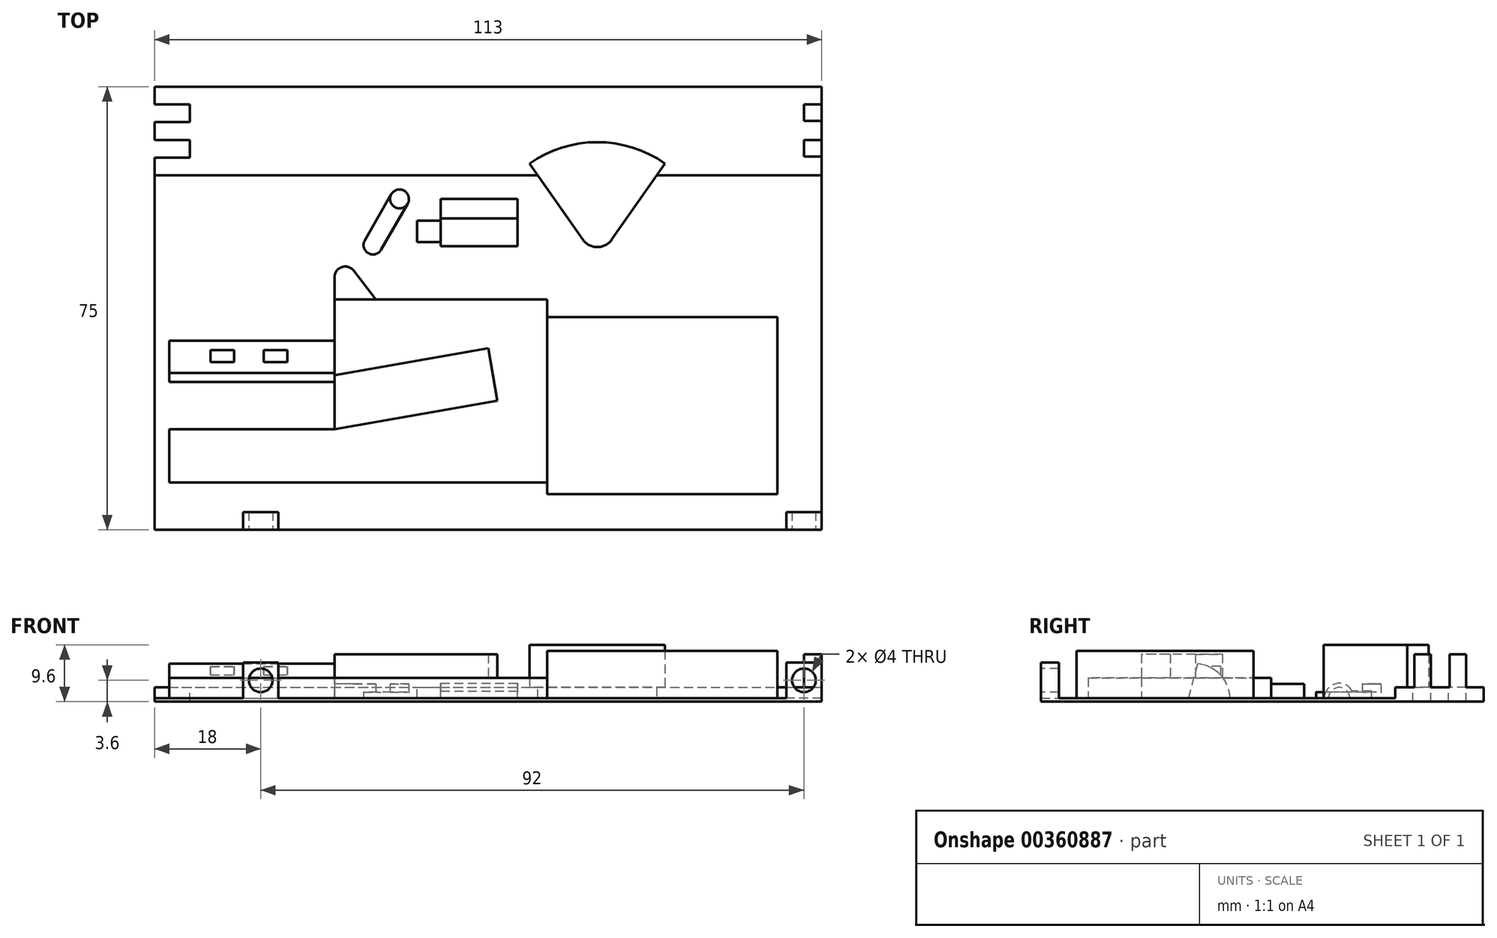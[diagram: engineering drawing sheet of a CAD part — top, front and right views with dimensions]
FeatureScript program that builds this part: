
annotation { "Feature Type Name" : "Feature", "Feature Type Description" : "" }
export const myFeature = defineFeature(function(context is Context, id is Id, definition is map)
    precondition{}
    {
        {
            var Q0;
            Q0=qCreatedBy(makeId("Top.planeOp"),FACE);
            var sketch = newSketch(context, id + "F0", { "sketchPlane" : qUnion([Q0])});
            skLineSegment(sketch, "E0.bottom", {"start": v(-56.5, 75) * mm, "end": v(56.5, 75) * mm});
            skLineSegment(sketch, "E0.top", {"start": v(-56.5, 0) * mm, "end": v(56.5, 0) * mm});
            skLineSegment(sketch, "E0.left", {"start": v(-56.5, 75) * mm, "end": v(-56.5, 0) * mm});
            skLineSegment(sketch, "E0.right", {"start": v(56.5, 75) * mm, "end": v(56.5, 0) * mm});
            skPoint(sketch, "E1", {"position": v(0, 0) * mm});
            skSolve(sketch);
        }
        {
            var Q0;
            Q0 = qSketchRegion(id + "F0", true);
            extrude(context, id + "F1", {"entities" : qUnion([Q0]), "depth" : 0.6 * mm});
        }
        {
            var Q0;
            Q0=makeQuery(id+"F1.opExtrude","CAP_FACE",FACE,{"disambiguationData":[OSD([sQuery(id+"F0.wireOp",EDGE,"E0.bottom"),sQuery(id+"F0.wireOp",EDGE,"E0.top"),sQuery(id+"F0.wireOp",EDGE,"E0.left"),sQuery(id+"F0.wireOp",EDGE,"E0.right")])],"isStart":false});
            var sketch = newSketch(context, id + "F2", { "sketchPlane" : qUnion([Q0])});
            skLineSegment(sketch, "E2.bottom", {"start": v(-56.5, 75) * mm, "end": v(56.5, 75) * mm});
            skLineSegment(sketch, "E2.top", {"start": v(-56.5, 60) * mm, "end": v(56.5, 60) * mm});
            skLineSegment(sketch, "E2.left", {"start": v(-56.5, 75) * mm, "end": v(-56.5, 60) * mm});
            skLineSegment(sketch, "E2.right", {"start": v(56.5, 75) * mm, "end": v(56.5, 60) * mm});
            skSolve(sketch);
        }
        {
            var Q0;
            Q0 = qSketchRegion(id + "F2", true);
            extrude(context, id + "F3", {"entities" : qUnion([Q0]), "operationType" : NewBodyOperationType.ADD, "depth" : 1.8 * mm});
        }
        {
            var Q0;
            Q0=qCreatedBy(makeId("Right.planeOp"),FACE);
            cPlane(context, id + "F4", {"entities" : qUnion([Q0]), "cplaneType" : CPlaneType.OFFSET, "offset" : 10 * mm, "width" : 150 * mm, "height" : 150 * mm});
        }
        {
            var Q0;
            Q0=qCreatedBy(id+"F4.planeOp",FACE);
            var sketch = newSketch(context, id + "F5", { "sketchPlane" : qUnion([Q0])});
            skLineSegment(sketch, "E3", {"start": v(6, 0.6) * mm, "end": v(36, 0.6) * mm});
            skLineSegment(sketch, "E4", {"start": v(36, 0.6) * mm, "end": v(36, 8.6) * mm});
            skLineSegment(sketch, "E5", {"start": v(6, 8.6) * mm, "end": v(6, 0.6) * mm});
            skLineSegment(sketch, "E6", {"start": v(36, 8.6) * mm, "end": v(6, 8.6) * mm});
            skSolve(sketch);
        }
        {
            var Q0;
            Q0 = qSketchRegion(id + "F5", true);
            extrude(context, id + "F6", {"entities" : qUnion([Q0]), "operationType" : NewBodyOperationType.ADD, "depth" : 39 * mm});
        }
        {
            var Q0;
            Q0=makeQuery(id+"F1.opExtrude","CAP_FACE",FACE,{"disambiguationData":[OSD([sQuery(id+"F0.wireOp",EDGE,"E0.bottom"),sQuery(id+"F0.wireOp",EDGE,"E0.top"),sQuery(id+"F0.wireOp",EDGE,"E0.left"),sQuery(id+"F0.wireOp",EDGE,"E0.right")])],"isStart":false});
            var sketch = newSketch(context, id + "F7", { "sketchPlane" : qUnion([Q0])});
            skLineSegment(sketch, "E7", {"start": v(-54, 17) * mm, "end": v(-54, 8) * mm});
            skLineSegment(sketch, "E8", {"start": v(-54, 8) * mm, "end": v(10, 8) * mm});
            skLineSegment(sketch, "E9", {"start": v(10, 8) * mm, "end": v(10, 39) * mm});
            skLineSegment(sketch, "E10", {"start": v(10, 39) * mm, "end": v(-26, 39) * mm});
            skLineSegment(sketch, "E11", {"start": v(-26, 39) * mm, "end": v(-26, 17) * mm});
            skLineSegment(sketch, "E12", {"start": v(-26, 17) * mm, "end": v(-54, 17) * mm});
            skSolve(sketch);
        }
        {
            var Q0;
            Q0 = qSketchRegion(id + "F7", true);
            extrude(context, id + "F8", {"entities" : qUnion([Q0]), "operationType" : NewBodyOperationType.ADD, "depth" : 3.4 * mm});
        }
        {
            var Q0;
            Q0=makeQuery(id+"F8.opExtrude","CAP_FACE",FACE,{"disambiguationData":[OSD([sQuery(id+"F7.wireOp",EDGE,"E7"),sQuery(id+"F7.wireOp",EDGE,"E8"),sQuery(id+"F7.wireOp",EDGE,"E9"),sQuery(id+"F7.wireOp",EDGE,"uyQ6YQ2C-q6pP-OxL6-5fo1-xEx53bqn0l92"),sQuery(id+"F7.wireOp",EDGE,"j48iJAs0-QAIT-l2oA-MukY-UUH54dbWInNL"),sQuery(id+"F7.wireOp",EDGE,"E10"),sQuery(id+"F7.wireOp",EDGE,"E11"),sQuery(id+"F7.wireOp",EDGE,"E12")])],"isStart":false});
            var sketch = newSketch(context, id + "F9", { "sketchPlane" : qUnion([Q0])});
            skLineSegment(sketch, "E13", {"start": v(-26, 17) * mm, "end": v(-26, 26.14) * mm});
            skLineSegment(sketch, "E14", {"start": v(-26, 26.14) * mm, "end": v(0.01, 30.73) * mm});
            skLineSegment(sketch, "E15", {"start": v(0.01, 30.73) * mm, "end": v(1.57, 21.86) * mm});
            skLineSegment(sketch, "E16", {"start": v(1.57, 21.86) * mm, "end": v(-26, 17) * mm});
            skSolve(sketch);
        }
        {
            var Q0;
            Q0 = qSketchRegion(id + "F9", true);
            extrude(context, id + "F10", {"entities" : qUnion([Q0]), "operationType" : NewBodyOperationType.ADD, "depth" : 4 * mm});
        }
        {
            var Q0;
            Q0=makeQuery(id+"F1.opExtrude","CAP_FACE",FACE,{"disambiguationData":[OSD([sQuery(id+"F0.wireOp",EDGE,"E0.bottom"),sQuery(id+"F0.wireOp",EDGE,"E0.top"),sQuery(id+"F0.wireOp",EDGE,"E0.left"),sQuery(id+"F0.wireOp",EDGE,"E0.right")])],"isStart":false});
            var sketch = newSketch(context, id + "F11", { "sketchPlane" : qUnion([Q0])});
            skLineSegment(sketch, "E17", {"start": v(-19, 39) * mm, "end": v(-26, 39) * mm});
            skLineSegment(sketch, "E18", {"start": v(-26, 39) * mm, "end": v(-26, 42.75) * mm});
            skLineSegment(sketch, "E19", {"start": v(-22.78, 43.86) * mm, "end": v(-19, 39) * mm});
            skPoint(sketch, "E20.visualSharp", {"position": v(-26, 48) * mm});
            skArc(sketch, "E20.filletArc", {"start": v(-22.78, 43.86) * mm, "mid": v(-24.78, 44.46) * mm, "end": v(-26, 42.75) * mm});
            skSolve(sketch);
        }
        {
            var Q0;
            Q0 = qSketchRegion(id + "F11", true);
            extrude(context, id + "F12", {"entities" : qUnion([Q0]), "operationType" : NewBodyOperationType.ADD, "depth" : 2.4 * mm});
        }
        {
            var Q0;
            Q0=makeQuery(id+"F12.boolean.opBoolean","MERGE",FACE,{"derivedFrom":[makeQuery(id+"F10.boolean.opBoolean","MERGE",FACE,{"derivedFrom":[makeQuery(id+"F8.opExtrude","SWEPT_FACE",FACE,{"disambiguationData":[OSD([sQuery(id+"F7.wireOp",EDGE,"E11")])]}),makeQuery(id+"F10.opExtrude","SWEPT_FACE",FACE,{"disambiguationData":[OSD([sQuery(id+"F9.wireOp",EDGE,"E13")])]})]}),makeQuery(id+"F12.opExtrude","SWEPT_FACE",FACE,{"disambiguationData":[OSD([sQuery(id+"F11.wireOp",EDGE,"E18")])]})]});
            var sketch = newSketch(context, id + "F13", { "sketchPlane" : qUnion([Q0])});
            skLineSegment(sketch, "E21", {"start": v(-32, 0.6) * mm, "end": v(-25, 0.6) * mm});
            skLineSegment(sketch, "E22", {"start": v(-25, 0.6) * mm, "end": v(-26.55, 6.4) * mm});
            skArc(sketch, "E23", {"start": v(-26.55, 6.4) * mm, "mid": v(-30.37, 4.53) * mm, "end": v(-32, 0.6) * mm});
            skSolve(sketch);
        }
        {
            var Q0;
            Q0 = qSketchRegion(id + "F13", true);
            extrude(context, id + "F14", {"entities" : qUnion([Q0]), "operationType" : NewBodyOperationType.ADD, "depth" : 28 * mm});
        }
        {
            var Q0;
            Q0=makeQuery(id+"F1.opExtrude","CAP_FACE",FACE,{"disambiguationData":[OSD([sQuery(id+"F0.wireOp",EDGE,"E0.bottom"),sQuery(id+"F0.wireOp",EDGE,"E0.top"),sQuery(id+"F0.wireOp",EDGE,"E0.left"),sQuery(id+"F0.wireOp",EDGE,"E0.right")])],"isStart":false});
            var sketch = newSketch(context, id + "F15", { "sketchPlane" : qUnion([Q0])});
            skLineSegment(sketch, "E24.bottom", {"start": v(-47, 30.4) * mm, "end": v(-43, 30.4) * mm});
            skLineSegment(sketch, "E24.top", {"start": v(-47, 28.4) * mm, "end": v(-43, 28.4) * mm});
            skLineSegment(sketch, "E24.left", {"start": v(-47, 30.4) * mm, "end": v(-47, 28.4) * mm});
            skLineSegment(sketch, "E24.right", {"start": v(-43, 30.4) * mm, "end": v(-43, 28.4) * mm});
            skLineSegment(sketch, "E25.bottom", {"start": v(-38, 30.4) * mm, "end": v(-34, 30.4) * mm});
            skLineSegment(sketch, "E25.top", {"start": v(-38, 28.4) * mm, "end": v(-34, 28.4) * mm});
            skLineSegment(sketch, "E25.left", {"start": v(-38, 30.4) * mm, "end": v(-38, 28.4) * mm});
            skLineSegment(sketch, "E25.right", {"start": v(-34, 30.4) * mm, "end": v(-34, 28.4) * mm});
            skSolve(sketch);
        }
        {
            var Q0;
            Q0 = qSketchRegion(id + "F15", true);
            extrude(context, id + "F16", {"entities" : qUnion([Q0]), "operationType" : NewBodyOperationType.ADD, "depth" : 5.4 * mm});
        }
        {
            var Q0;
            Q0=makeQuery(id+"F1.opExtrude","CAP_FACE",FACE,{"disambiguationData":[OSD([sQuery(id+"F0.wireOp",EDGE,"E0.bottom"),sQuery(id+"F0.wireOp",EDGE,"E0.top"),sQuery(id+"F0.wireOp",EDGE,"E0.left"),sQuery(id+"F0.wireOp",EDGE,"E0.right")])],"isStart":false});
            var sketch = newSketch(context, id + "F17", { "sketchPlane" : qUnion([Q0])});
            skLineSegment(sketch, "E26", {"start": v(29.97, 62) * mm, "end": v(18.5, 45.62) * mm});
            skLineSegment(sketch, "E27", {"start": v(18.5, 45.62) * mm, "end": v(7.03, 62) * mm});
            skArc(sketch, "E28", {"start": v(29.97, 62) * mm, "mid": v(18.5, 65.62) * mm, "end": v(7.03, 62) * mm});
            skSolve(sketch);
        }
        {
            var Q0;
            Q0 = qSketchRegion(id + "F17", true);
            extrude(context, id + "F18", {"entities" : qUnion([Q0]), "operationType" : NewBodyOperationType.ADD, "depth" : 9 * mm});
        }
        {
            var Q0;
            Q0=makeQuery(id+"F18.opExtrude","SWEPT_EDGE",EDGE,{"disambiguationData":[OSD([sQuery(id+"F17.wireOp",EDGE,"E26"),sQuery(id+"F17.wireOp",EDGE,"E27")])]});
            fillet(context, id + "F19", {"entities" : qUnion([Q0]), "radius" : 3 * mm, "tangentPropagation" : true, "allowEdgeOverflow" : false});
        }
        {
            var Q0;
            Q0=qCreatedBy(makeId("Right.planeOp"),FACE);
            cPlane(context, id + "F20", {"entities" : qUnion([Q0]), "cplaneType" : CPlaneType.OFFSET, "offset" : 5 * mm, "width" : 150 * mm, "height" : 150 * mm});
        }
        {
            var Q0;
            Q0=qCreatedBy(id+"F20.planeOp",FACE);
            var sketch = newSketch(context, id + "F21", { "sketchPlane" : qUnion([Q0])});
            skArc(sketch, "E29", {"start": v(52.93, 0) * mm, "mid": v(50.5, 3.1) * mm, "end": v(48.07, 0) * mm});
            skLineSegment(sketch, "E30", {"start": v(53, 0.6) * mm, "end": v(56, 0.6) * mm});
            skLineSegment(sketch, "E31", {"start": v(56, 0.6) * mm, "end": v(56, 1.8) * mm});
            skLineSegment(sketch, "E32", {"start": v(56, 1.8) * mm, "end": v(52.7, 1.8) * mm});
            skLineSegment(sketch, "E33", {"start": v(48.07, 0) * mm, "end": v(52.93, 0) * mm});
            skSolve(sketch);
        }
        {
            var Q0;
            Q0 = qSketchRegion(id + "F21", true);
            extrude(context, id + "F22", {"entities" : qUnion([Q0]), "operationType" : NewBodyOperationType.ADD, "oppositeDirection" : true, "depth" : 13 * mm});
        }
        {
            var Q0;
            Q0=makeQuery(id+"F22.opExtrude","CAP_FACE",FACE,{"disambiguationData":[OSD([sQuery(id+"F21.wireOp",EDGE,"E29"),sQuery(id+"F21.wireOp",EDGE,"E30"),sQuery(id+"F21.wireOp",EDGE,"E31"),sQuery(id+"F21.wireOp",EDGE,"E32")])],"isStart":false});
            var sketch = newSketch(context, id + "F23", { "sketchPlane" : qUnion([Q0])});
            skArc(sketch, "E34", {"start": v(-48.8, 0) * mm, "mid": v(-50.5, 2.4) * mm, "end": v(-52.2, 0) * mm});
            skLineSegment(sketch, "E35", {"start": v(-48.8, 0) * mm, "end": v(-52.2, 0) * mm});
            skSolve(sketch);
        }
        {
            var Q0;
            Q0 = qSketchRegion(id + "F23", true);
            extrude(context, id + "F24", {"entities" : qUnion([Q0]), "operationType" : NewBodyOperationType.ADD, "depth" : 4 * mm});
        }
        {
            var Q0;
            Q0=makeQuery(id+"F1.opExtrude","CAP_FACE",FACE,{"disambiguationData":[OSD([sQuery(id+"F0.wireOp",EDGE,"E0.bottom"),sQuery(id+"F0.wireOp",EDGE,"E0.top"),sQuery(id+"F0.wireOp",EDGE,"E0.left"),sQuery(id+"F0.wireOp",EDGE,"E0.right")])],"isStart":false});
            var sketch = newSketch(context, id + "F25", { "sketchPlane" : qUnion([Q0])});
            skCircle(sketch, "E36", {"center": v(-15, 56) * mm, "radius": 1.6 * mm});
            skSolve(sketch);
        }
        {
            var Q0;
            Q0 = qSketchRegion(id + "F25", true);
            extrude(context, id + "F26", {"entities" : qUnion([Q0]), "operationType" : NewBodyOperationType.ADD, "depth" : 2.4 * mm});
        }
        {
            var Q0;
            Q0=makeQuery(id+"F1.opExtrude","CAP_FACE",FACE,{"disambiguationData":[OSD([sQuery(id+"F0.wireOp",EDGE,"E0.bottom"),sQuery(id+"F0.wireOp",EDGE,"E0.top"),sQuery(id+"F0.wireOp",EDGE,"E0.left"),sQuery(id+"F0.wireOp",EDGE,"E0.right")])],"isStart":false});
            var sketch = newSketch(context, id + "F27", { "sketchPlane" : qUnion([Q0])});
            skLineSegment(sketch, "E37", {"start": v(-16.39, 56.8) * mm, "end": v(-20.87, 49) * mm});
            skLineSegment(sketch, "E38", {"start": v(-13.61, 55.2) * mm, "end": v(-18.1, 47.4) * mm});
            skArc(sketch, "E39", {"start": v(-20.87, 49) * mm, "mid": v(-20.28, 46.81) * mm, "end": v(-18.1, 47.4) * mm});
            skArc(sketch, "E40", {"start": v(-16.39, 56.8) * mm, "mid": v(-14.2, 57.39) * mm, "end": v(-13.61, 55.2) * mm});
            skSolve(sketch);
        }
        {
            var Q0;
            Q0 = qSketchRegion(id + "F27", true);
            extrude(context, id + "F28", {"entities" : qUnion([Q0]), "operationType" : NewBodyOperationType.ADD, "depth" : 1 * mm});
        }
        {
            var Q0;
            Q0=makeQuery(id+"F3.opExtrude","CAP_FACE",FACE,{"disambiguationData":[OSD([sQuery(id+"F2.wireOp",EDGE,"E2.bottom"),sQuery(id+"F2.wireOp",EDGE,"E2.top"),sQuery(id+"F2.wireOp",EDGE,"E2.left"),sQuery(id+"F2.wireOp",EDGE,"E2.right")])],"isStart":false});
            var sketch = newSketch(context, id + "F29", { "sketchPlane" : qUnion([Q0])});
            skLineSegment(sketch, "E41.bottom", {"start": v(53.5, 72) * mm, "end": v(56.5, 72) * mm});
            skLineSegment(sketch, "E41.top", {"start": v(53.5, 69.2) * mm, "end": v(56.5, 69.2) * mm});
            skLineSegment(sketch, "E41.left", {"start": v(53.5, 72) * mm, "end": v(53.5, 69.2) * mm});
            skLineSegment(sketch, "E41.right", {"start": v(56.5, 72) * mm, "end": v(56.5, 69.2) * mm});
            skLineSegment(sketch, "E42.bottom", {"start": v(53.5, 66) * mm, "end": v(56.5, 66) * mm});
            skLineSegment(sketch, "E42.top", {"start": v(53.5, 63.2) * mm, "end": v(56.5, 63.2) * mm});
            skLineSegment(sketch, "E42.left", {"start": v(53.5, 66) * mm, "end": v(53.5, 63.2) * mm});
            skLineSegment(sketch, "E42.right", {"start": v(56.5, 66) * mm, "end": v(56.5, 63.2) * mm});
            skSolve(sketch);
        }
        {
            var Q0;
            Q0 = qSketchRegion(id + "F29", true);
            extrude(context, id + "F30", {"entities" : qUnion([Q0]), "operationType" : NewBodyOperationType.ADD, "depth" : 5.6 * mm});
        }
        {
            var Q0;
            Q0=makeQuery(id+"F3.opExtrude","CAP_FACE",FACE,{"disambiguationData":[OSD([sQuery(id+"F2.wireOp",EDGE,"E2.bottom"),sQuery(id+"F2.wireOp",EDGE,"E2.top"),sQuery(id+"F2.wireOp",EDGE,"E2.left"),sQuery(id+"F2.wireOp",EDGE,"E2.right")])],"isStart":false});
            var sketch = newSketch(context, id + "F31", { "sketchPlane" : qUnion([Q0])});
            skLineSegment(sketch, "E43.bottom", {"start": v(-56.5, 72) * mm, "end": v(-50.5, 72) * mm});
            skLineSegment(sketch, "E43.top", {"start": v(-56.5, 69) * mm, "end": v(-50.5, 69) * mm});
            skLineSegment(sketch, "E43.left", {"start": v(-56.5, 72) * mm, "end": v(-56.5, 69) * mm});
            skLineSegment(sketch, "E43.right", {"start": v(-50.5, 72) * mm, "end": v(-50.5, 69) * mm});
            skLineSegment(sketch, "E44.bottom", {"start": v(-56.5, 66) * mm, "end": v(-50.5, 66) * mm});
            skLineSegment(sketch, "E44.top", {"start": v(-56.5, 63) * mm, "end": v(-50.5, 63) * mm});
            skLineSegment(sketch, "E44.left", {"start": v(-56.5, 66) * mm, "end": v(-56.5, 63) * mm});
            skLineSegment(sketch, "E44.right", {"start": v(-50.5, 66) * mm, "end": v(-50.5, 63) * mm});
            skSolve(sketch);
        }
        {
            var Q0;
            Q0 = qSketchRegion(id + "F31", true);
            extrude(context, id + "F32", {"entities" : qUnion([Q0]), "operationType" : NewBodyOperationType.REMOVE, "oppositeDirection" : true, "depth" : 3 * mm});
        }
        {
            var Q0;
            Q0=makeQuery(id+"F1.opExtrude","CAP_FACE",FACE,{"disambiguationData":[OSD([sQuery(id+"F0.wireOp",EDGE,"E0.bottom"),sQuery(id+"F0.wireOp",EDGE,"E0.top"),sQuery(id+"F0.wireOp",EDGE,"E0.left"),sQuery(id+"F0.wireOp",EDGE,"E0.right")])],"isStart":false});
            var sketch = newSketch(context, id + "F33", { "sketchPlane" : qUnion([Q0])});
            skLineSegment(sketch, "E45.bottom", {"start": v(56.5, 0) * mm, "end": v(50.5, 0) * mm});
            skLineSegment(sketch, "E45.top", {"start": v(56.5, 3) * mm, "end": v(50.5, 3) * mm});
            skLineSegment(sketch, "E45.left", {"start": v(56.5, 0) * mm, "end": v(56.5, 3) * mm});
            skLineSegment(sketch, "E45.right", {"start": v(50.5, 0) * mm, "end": v(50.5, 3) * mm});
            skLineSegment(sketch, "E46.bottom", {"start": v(-41.5, 0) * mm, "end": v(-35.5, 0) * mm});
            skLineSegment(sketch, "E46.top", {"start": v(-41.5, 3) * mm, "end": v(-35.5, 3) * mm});
            skLineSegment(sketch, "E46.left", {"start": v(-41.5, 0) * mm, "end": v(-41.5, 3) * mm});
            skLineSegment(sketch, "E46.right", {"start": v(-35.5, 0) * mm, "end": v(-35.5, 3) * mm});
            skSolve(sketch);
        }
        {
            var Q0;
            Q0 = qSketchRegion(id + "F33", true);
            extrude(context, id + "F34", {"entities" : qUnion([Q0]), "operationType" : NewBodyOperationType.ADD, "depth" : 6 * mm});
        }
        {
            var Q0;
            Q0=makeQuery(id+"F34.boolean.opBoolean","MERGE",FACE,{"derivedFrom":[makeQuery(id+"F1.opExtrude","SWEPT_FACE",FACE,{"disambiguationData":[OSD([sQuery(id+"F0.wireOp",EDGE,"E0.top")])]}),makeQuery(id+"F34.opExtrude","SWEPT_FACE",FACE,{"disambiguationData":[OSD([sQuery(id+"F33.wireOp",EDGE,"E45.bottom")])]}),makeQuery(id+"F34.opExtrude","SWEPT_FACE",FACE,{"disambiguationData":[OSD([sQuery(id+"F33.wireOp",EDGE,"E46.bottom")])]})]});
            var sketch = newSketch(context, id + "F35", { "sketchPlane" : qUnion([Q0])});
            skCircle(sketch, "E47", {"center": v(53.5, 3.6) * mm, "radius": 2 * mm});
            skCircle(sketch, "E48", {"center": v(-38.5, 3.6) * mm, "radius": 2 * mm});
            skSolve(sketch);
        }
        {
            var Q0;
            Q0 = qSketchRegion(id + "F35", true);
            extrude(context, id + "F36", {"entities" : qUnion([Q0]), "operationType" : NewBodyOperationType.REMOVE, "oppositeDirection" : true, "depth" : 4 * mm});
        }
    });
